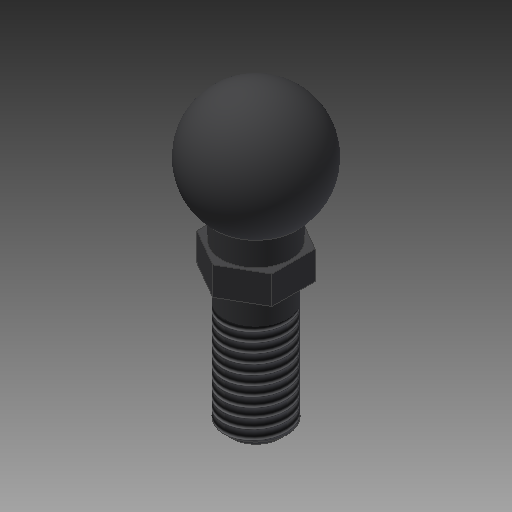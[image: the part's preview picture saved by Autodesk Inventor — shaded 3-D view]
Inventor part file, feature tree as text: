
AUTODESK INVENTOR PART (.ipt)
format: ipt  version: 2018 (Build 220112000, 112)  size: 161,792 bytes
history: native  units: mm
features: other x7, sketch x2, revolve x1, thread x1, extrude x1
ambient origin geometry x8: Origin, YZ Plane, XZ Plane, XY Plane, X Axis, Y Axis, Z Axis, Center Point
bodies: Solid1 (feature_tree)
feature tree (12):
  revolve  "Revolution1"  [1 undecoded]
  thread  "Thread1"  [1 undecoded]
  extrude  "Extrusion1"  [1 undecoded]
  other  "IP1_XY"
  other  "IP1_YZ"
  other  "IP1_ZX"
  other  "IP1_X"
  other  "IP1_Y"
  other  "IP1_Z"
  other  "IP1_Center"
  sketch  "Sketch_2"  dims[d0=360.0deg d1=16.0mm d2=0.0mm d3=4.5mm d4=0.0mm]
  sketch  "Sketch_3"
note: 3 required parameter values undecoded (feature->parameter linkage not recoverable at this tier; creation-order binding heuristic only, values carry confidence <= 0.55)